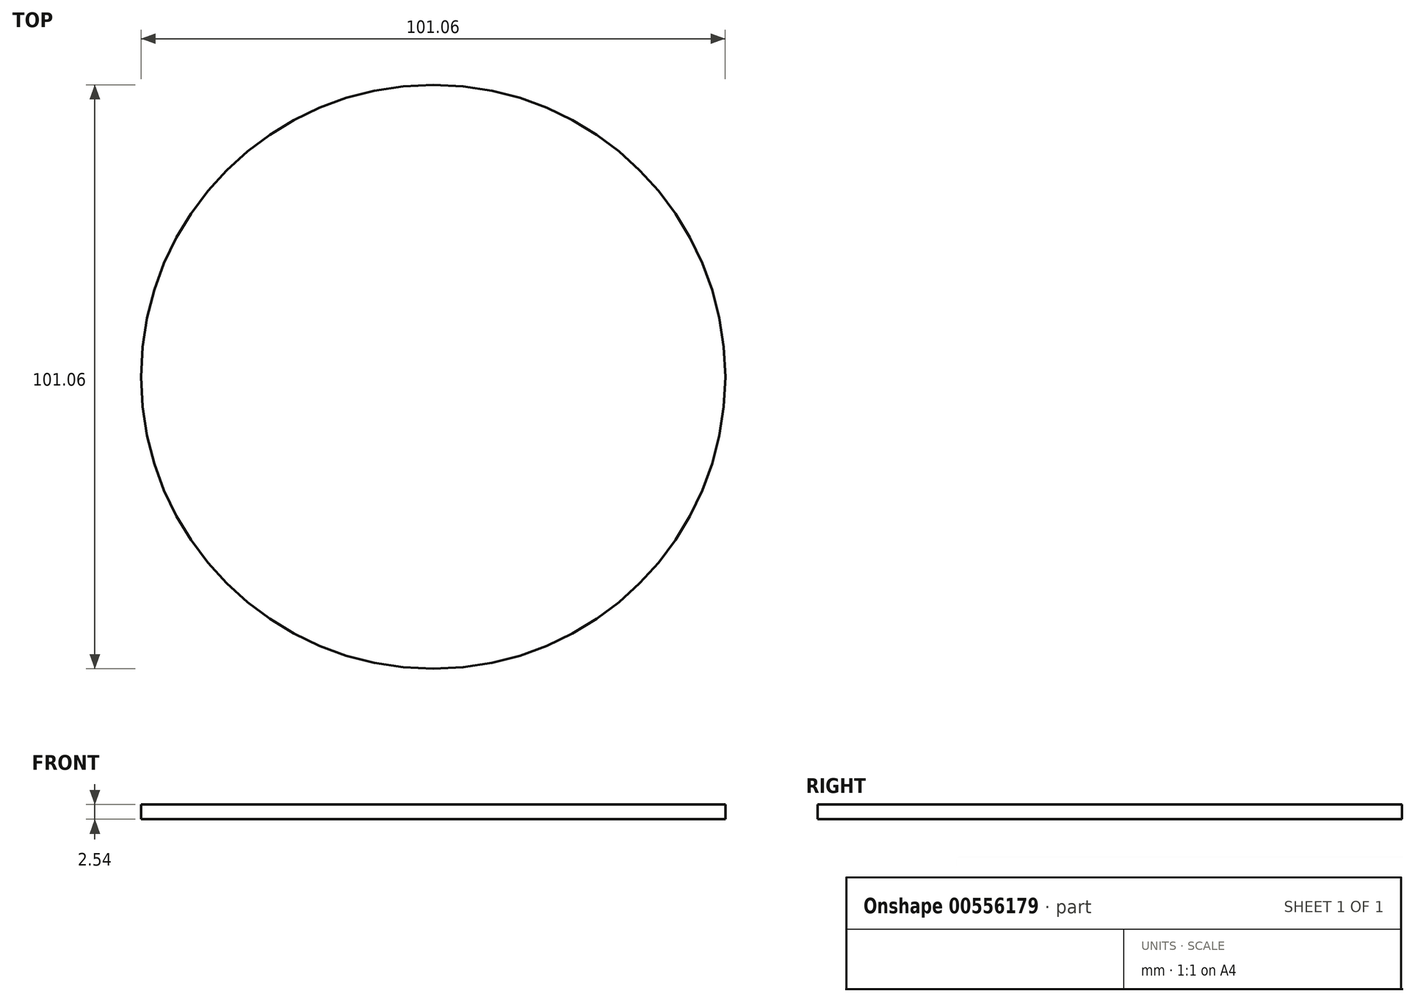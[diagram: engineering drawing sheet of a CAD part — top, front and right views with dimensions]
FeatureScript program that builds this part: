
annotation { "Feature Type Name" : "Feature", "Feature Type Description" : "" }
export const myFeature = defineFeature(function(context is Context, id is Id, definition is map)
    precondition{}
    {
        {
            var Q0;
            Q0=qCreatedBy(makeId("Top.planeOp"),FACE);
            var sketch = newSketch(context, id + "F0", { "sketchPlane" : qUnion([Q0])});
            skCircle(sketch, "E0", {"center": v(0, 0) * mm, "radius": 50.53 * mm});
            skSolve(sketch);
        }
        {
            var Q0;
            Q0 = qSketchRegion(id + "F0", true);
            extrude(context, id + "F1", {"entities" : qUnion([Q0]), "depth" : 2.54 * mm, "offsetDistance" : 25.4 * mm});
        }
    });
